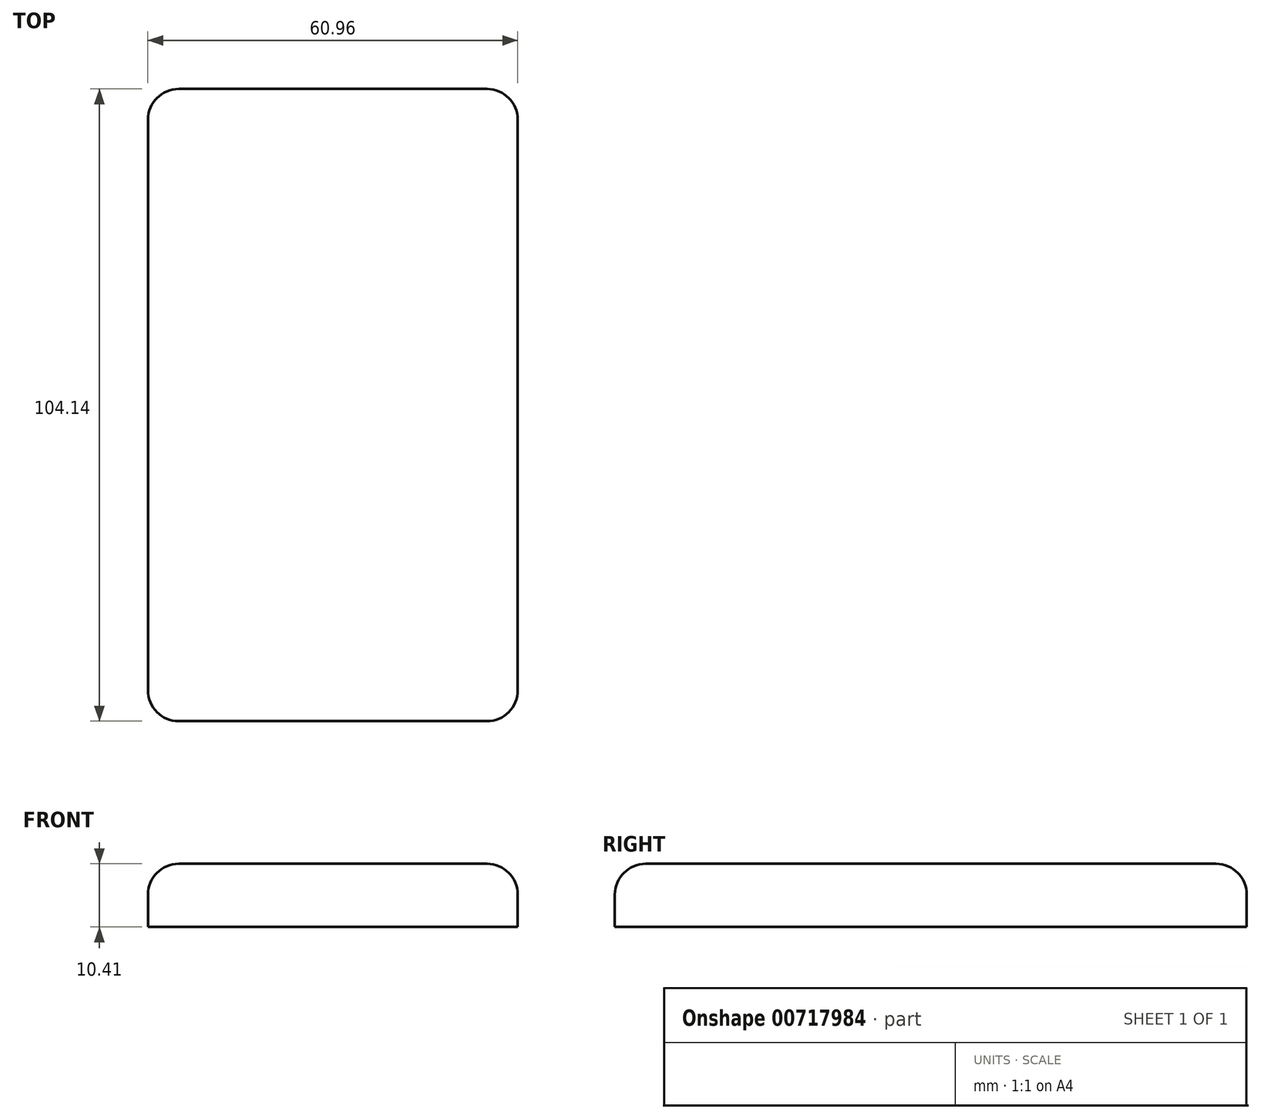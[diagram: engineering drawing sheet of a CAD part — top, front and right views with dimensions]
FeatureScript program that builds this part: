
annotation { "Feature Type Name" : "Feature", "Feature Type Description" : "" }
export const myFeature = defineFeature(function(context is Context, id is Id, definition is map)
    precondition{}
    {
        {
            var Q0;
            Q0=qCreatedBy(makeId("Top.planeOp"),FACE);
            var sketch = newSketch(context, id + "F0", { "sketchPlane" : qUnion([Q0])});
            skLineSegment(sketch, "E0.bottom", {"start": v(-61.62, 14.82) * mm, "end": v(-10.82, 14.82) * mm});
            skLineSegment(sketch, "E0.top", {"start": v(-61.62, -89.32) * mm, "end": v(-10.82, -89.32) * mm});
            skLineSegment(sketch, "E0.left", {"start": v(-66.7, 9.74) * mm, "end": v(-66.7, -84.24) * mm});
            skLineSegment(sketch, "E0.right", {"start": v(-5.74, 9.74) * mm, "end": v(-5.74, -84.24) * mm});
            skPoint(sketch, "E0.middle", {"position": v(-36.22, -37.25) * mm});
            skLineSegment(sketch, "E1.bottom", {"start": v(-61.62, 8.47) * mm, "end": v(-10.82, 8.47) * mm});
            skLineSegment(sketch, "E1.top", {"start": v(-61.62, -29.63) * mm, "end": v(-10.82, -29.63) * mm});
            skLineSegment(sketch, "E1.left", {"start": v(-61.62, 8.47) * mm, "end": v(-61.62, -29.63) * mm});
            skLineSegment(sketch, "E1.right", {"start": v(-10.82, 8.47) * mm, "end": v(-10.82, -29.63) * mm});
            skPoint(sketch, "E1.middle", {"position": v(-36.22, -10.58) * mm});
            skCircle(sketch, "E2", {"center": v(-36.22, -58.84) * mm, "radius": 17.78 * mm});
            skCircle(sketch, "E3", {"center": v(-36.22, -58.84) * mm, "radius": 7.62 * mm});
            skPoint(sketch, "E4.visualSharp", {"position": v(-5.74, 14.82) * mm});
            skArc(sketch, "E4.filletArc", {"start": v(-5.74, 9.74) * mm, "mid": v(-7.23, 13.33) * mm, "end": v(-10.82, 14.82) * mm});
            skPoint(sketch, "E5.visualSharp", {"position": v(-66.7, 14.82) * mm});
            skArc(sketch, "E5.filletArc", {"start": v(-61.62, 14.82) * mm, "mid": v(-65.2, 13.33) * mm, "end": v(-66.7, 9.74) * mm});
            skPoint(sketch, "E6.visualSharp", {"position": v(-66.7, -89.32) * mm});
            skArc(sketch, "E6.filletArc", {"start": v(-66.7, -84.24) * mm, "mid": v(-65.2, -87.83) * mm, "end": v(-61.62, -89.32) * mm});
            skPoint(sketch, "E7.visualSharp", {"position": v(-5.74, -89.32) * mm});
            skArc(sketch, "E7.filletArc", {"start": v(-10.82, -89.32) * mm, "mid": v(-7.23, -87.83) * mm, "end": v(-5.74, -84.24) * mm});
            skSolve(sketch);
        }
        {
            var Q0;
            Q0 = qSketchRegion(id + "F0", true);
            var Q1;
            Q1=makeQuery(id+"F0.imprint","IMPRINT",FACE,{"disambiguationData":[TD([[makeQuery(id+"F0.imprint","IMPRINT",EDGE,{"derivedFrom":sQuery(id+"F0.wireOp",EDGE,"E1.bottom")}),-1.0]])]});
            var Q2;
            Q2=makeQuery(id+"F0.imprint","IMPRINT",FACE,{"disambiguationData":[TD([[makeQuery(id+"F0.imprint","IMPRINT",EDGE,{"derivedFrom":sQuery(id+"F0.wireOp",EDGE,"E2")}),1.0]])]});
            var Q3;
            Q3=makeQuery(id+"F0.imprint","IMPRINT",FACE,{"disambiguationData":[TD([[makeQuery(id+"F0.imprint","IMPRINT",EDGE,{"derivedFrom":sQuery(id+"F0.wireOp",EDGE,"E3")}),1.0]])]});
            extrude(context, id + "F1", {"entities" : qUnion([Q0, Q1, Q2, Q3]), "depth" : 10.4 * mm, "offsetDistance" : 25 * mm});
        }
        {
            var Q0;
            Q0=makeQuery(id+"F1.opExtrude","CAP_EDGE",EDGE,{"disambiguationData":[OSD([sQuery(id+"F0.wireOp",EDGE,"E0.top")])],"isStart":false});
            var Q1;
            Q1=makeQuery(id+"F1.opExtrude","CAP_EDGE",EDGE,{"disambiguationData":[OSD([sQuery(id+"F0.wireOp",EDGE,"E0.bottom")])],"isStart":false});
            fillet(context, id + "F2", {"entities" : qUnion([Q0, Q1]), "radius" : 5.08 * mm, "tangentPropagation" : true, "allowEdgeOverflow" : false});
        }
    });
